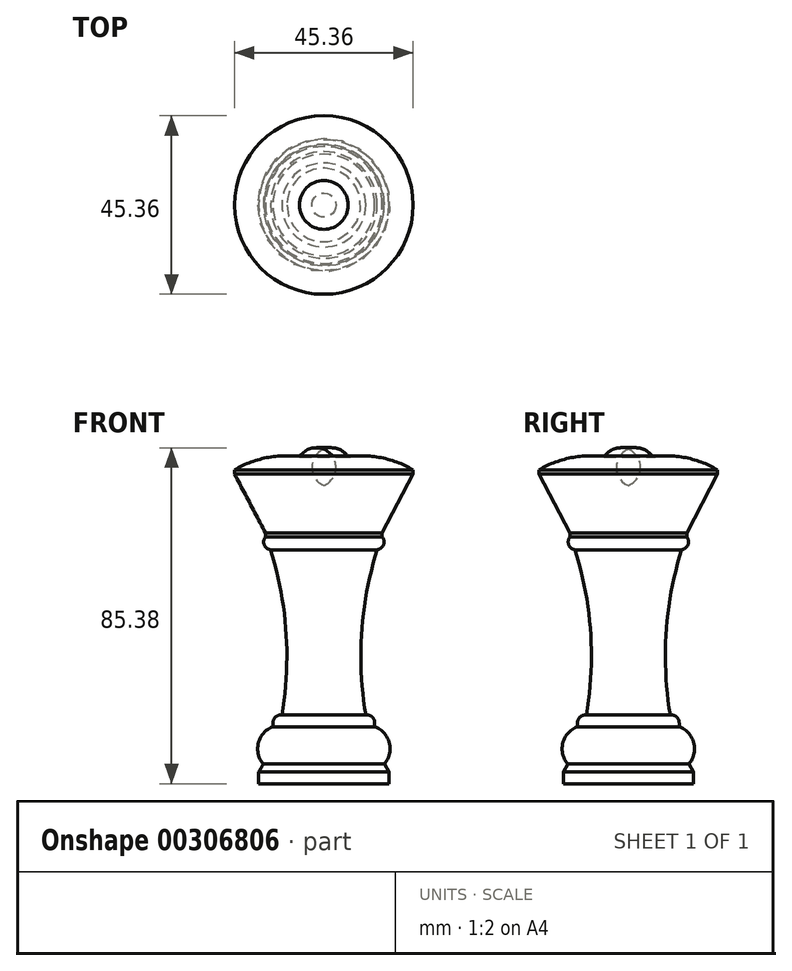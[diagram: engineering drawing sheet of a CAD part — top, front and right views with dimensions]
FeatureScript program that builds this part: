
annotation { "Feature Type Name" : "Feature", "Feature Type Description" : "" }
export const myFeature = defineFeature(function(context is Context, id is Id, definition is map)
    precondition{}
    {
        {
            var Q0;
            Q0=qCreatedBy(makeId("Front.planeOp"),FACE);
            var sketch = newSketch(context, id + "F0", { "sketchPlane" : qUnion([Q0])});
            skArc(sketch, "E0", {"start": v(6.19, -2) * mm, "mid": v(3.46, 0.14) * mm, "end": v(0, 0) * mm});
            skArc(sketch, "E1", {"start": v(22.68, -5.27) * mm, "mid": v(14.72, -2.18) * mm, "end": v(6.19, -2) * mm});
            skLineSegment(sketch, "E2", {"start": v(22.68, -5.27) * mm, "end": v(22.68, -6.27) * mm});
            skLineSegment(sketch, "E3", {"start": v(22.68, -6.27) * mm, "end": v(14.83, -21.27) * mm});
            skLineSegment(sketch, "E4", {"start": v(14.83, -21.27) * mm, "end": v(14.83, -22.27) * mm});
            skArc(sketch, "E5", {"start": v(13.54, -25.53) * mm, "mid": v(15.15, -24.28) * mm, "end": v(14.83, -22.27) * mm});
            skLineSegment(sketch, "E6", {"start": v(12.92, -69.5) * mm, "end": v(12.92, -70.5) * mm});
            skArc(sketch, "E7", {"start": v(15.39, -80) * mm, "mid": v(16.63, -74.6) * mm, "end": v(12.92, -70.5) * mm});
            skLineSegment(sketch, "E8", {"start": v(15.39, -80) * mm, "end": v(16.54, -82) * mm});
            skLineSegment(sketch, "E9", {"start": v(16.54, -82) * mm, "end": v(16.54, -85) * mm});
            skLineSegment(sketch, "E10", {"start": v(16.54, -85) * mm, "end": v(0, -85) * mm});
            skLineSegment(sketch, "E11", {"start": v(0, -85) * mm, "end": v(0, 0) * mm});
            skArc(sketch, "E12", {"start": v(12.92, -69.5) * mm, "mid": v(12.24, -67.99) * mm, "end": v(10.66, -67.5) * mm});
            skArc(sketch, "E13", {"start": v(13.54, -25.53) * mm, "mid": v(9.61, -46.35) * mm, "end": v(10.66, -67.5) * mm});
            skSolve(sketch);
        }
        {
            var Q0;
            Q0=makeQuery(id+"F0.imprint","IMPRINT",FACE,{"disambiguationData":[TD([[makeQuery(id+"F0.imprint","IMPRINT",EDGE,{"derivedFrom":sQuery(id+"F0.wireOp",EDGE,"E0")}),1.0]])]});
            var Q1;
            Q1=sQuery(id+"F0.wireOp",EDGE,"E11");
            revolve(context, id + "F1", {"entities" : qUnion([Q0]), "axis" : qUnion([Q1]), "revolveType" : RevolveType.FULL});
        }
    });
